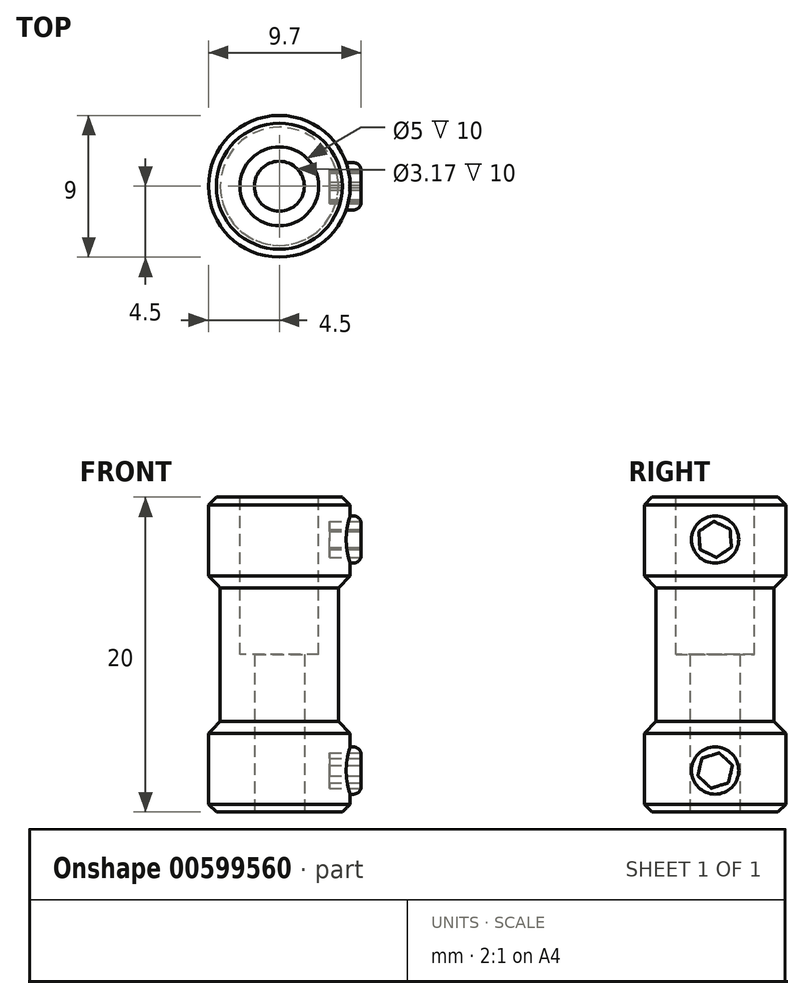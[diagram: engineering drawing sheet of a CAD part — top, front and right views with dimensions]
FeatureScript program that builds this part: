
annotation { "Feature Type Name" : "Feature", "Feature Type Description" : "" }
export const myFeature = defineFeature(function(context is Context, id is Id, definition is map)
    precondition{}
    {
        {
            var Q0;
            Q0=qCreatedBy(makeId("Top.planeOp"),FACE);
            var sketch = newSketch(context, id + "F0", { "sketchPlane" : qUnion([Q0])});
            skCircle(sketch, "E0", {"center": v(0, 0) * mm, "radius": 4.5 * mm});
            skSolve(sketch);
        }
        {
            var Q0;
            Q0 = qSketchRegion(id + "F0", true);
            extrude(context, id + "F1", {"entities" : qUnion([Q0]), "depth" : 20 * mm, "offsetDistance" : 25 * mm});
        }
        {
            var Q0;
            Q0=makeQuery(id+"F1.opExtrude","CAP_FACE",FACE,{"disambiguationData":[OSD([sQuery(id+"F0.wireOp",EDGE,"E0")])],"isStart":false});
            var sketch = newSketch(context, id + "F2", { "sketchPlane" : qUnion([Q0])});
            skCircle(sketch, "E1", {"center": v(0, 0) * mm, "radius": 2.5 * mm});
            skSolve(sketch);
        }
        {
            var Q0;
            Q0 = qSketchRegion(id + "F2", true);
            extrude(context, id + "F3", {"entities" : qUnion([Q0]), "operationType" : NewBodyOperationType.REMOVE, "oppositeDirection" : true, "depth" : 10 * mm, "offsetDistance" : 25 * mm});
        }
        {
            var Q0;
            Q0=makeQuery(id+"F1.opExtrude","CAP_FACE",FACE,{"disambiguationData":[OSD([sQuery(id+"F0.wireOp",EDGE,"E0")])],"isStart":true});
            var sketch = newSketch(context, id + "F4", { "sketchPlane" : qUnion([Q0])});
            skCircle(sketch, "E2", {"center": v(0, 0) * mm, "radius": 1.59 * mm});
            skSolve(sketch);
        }
        {
            var Q0;
            Q0 = qSketchRegion(id + "F4", true);
            extrude(context, id + "F5", {"entities" : qUnion([Q0]), "operationType" : NewBodyOperationType.REMOVE, "oppositeDirection" : true, "depth" : 10 * mm, "offsetDistance" : 25 * mm});
        }
        {
            var Q0;
            Q0=makeQuery(id+"F1.opExtrude","CAP_FACE",FACE,{"disambiguationData":[OSD([sQuery(id+"F0.wireOp",EDGE,"E0")])],"isStart":true});
            var sketch = newSketch(context, id + "F6", { "sketchPlane" : qUnion([Q0])});
            skCircle(sketch, "E3", {"center": v(0, 0) * mm, "radius": 3.75 * mm});
            skCircle(sketch, "E4", {"center": v(0, 0) * mm, "radius": 8.33 * mm});
            skSolve(sketch);
        }
        {
            var Q0;
            Q0 = qSketchRegion(id + "F6", true);
            extrude(context, id + "F7", {"entities" : qUnion([Q0]), "operationType" : NewBodyOperationType.REMOVE, "oppositeDirection" : true, "depth" : 14 * mm, "offsetDistance" : 25 * mm, "hasSecondDirection" : true, "secondDirectionOppositeDirection" : true, "secondDirectionDepth" : 6 * mm});
        }
        {
            var Q0;
            Q0=makeQuery(id+"F7.boolean.opBoolean","INTERSECT",EDGE,{"derivedFrom":[makeQuery(id+"F1.opExtrude","SWEPT_FACE",FACE,{"disambiguationData":[OSD([sQuery(id+"F0.wireOp",EDGE,"E0")])]}),makeQuery(id+"F7.opExtrude","CAP_FACE",FACE,{"disambiguationData":[OSD([sQuery(id+"F6.wireOp",EDGE,"E3"),sQuery(id+"F6.wireOp",EDGE,"E4")])],"isStart":false})]});
            var Q1;
            Q1=makeQuery(id+"F7.boolean.opBoolean","INTERSECT",EDGE,{"derivedFrom":[makeQuery(id+"F1.opExtrude","SWEPT_FACE",FACE,{"disambiguationData":[OSD([sQuery(id+"F0.wireOp",EDGE,"E0")])]}),makeQuery(id+"F7.opExtrude","CAP_FACE",FACE,{"disambiguationData":[OSD([sQuery(id+"F6.wireOp",EDGE,"E3"),sQuery(id+"F6.wireOp",EDGE,"E4")])],"isStart":true})]});
            chamfer(context, id + "F8", {"entities" : qUnion([Q0, Q1]), "width" : 1 * mm, "tangentPropagation" : true});
        }
        {
            var Q0;
            Q0=makeQuery(id+"F1.opExtrude","CAP_EDGE",EDGE,{"disambiguationData":[OSD([sQuery(id+"F0.wireOp",EDGE,"E0")])],"isStart":false});
            var Q1;
            Q1=makeQuery(id+"F1.opExtrude","CAP_EDGE",EDGE,{"disambiguationData":[OSD([sQuery(id+"F0.wireOp",EDGE,"E0")])],"isStart":true});
            chamfer(context, id + "F9", {"entities" : qUnion([Q0, Q1]), "width" : 0.5 * mm, "tangentPropagation" : true});
        }
        {
            var Q0;
            Q0=qCreatedBy(makeId("Right.planeOp"),FACE);
            var sketch = newSketch(context, id + "F10", { "sketchPlane" : qUnion([Q0])});
            skCircle(sketch, "E5", {"center": v(0, 17.31) * mm, "radius": 1.5 * mm});
            skCircle(sketch, "E6", {"center": v(0, 2.64) * mm, "radius": 1.5 * mm});
            skSolve(sketch);
        }
        {
            var Q0;
            Q0 = qSketchRegion(id + "F10", true);
            extrude(context, id + "F11", {"entities" : qUnion([Q0]), "operationType" : NewBodyOperationType.ADD, "depth" : 5.2 * mm, "offsetDistance" : 25 * mm, "hasSecondDirection" : true, "secondDirectionOppositeDirection" : false, "secondDirectionDepth" : 4 * mm});
        }
        {
            var Q0;
            Q0=makeQuery(id+"F11.opExtrude","CAP_FACE",FACE,{"disambiguationData":[OSD([sQuery(id+"F10.wireOp",EDGE,"E6")])],"isStart":false});
            var sketch = newSketch(context, id + "F12", { "sketchPlane" : qUnion([Q0])});
            skCircle(sketch, "E7.cCircle", {"center": v(0, 2.64) * mm, "radius": 1.15 * mm, "construction": true});
            skLineSegment(sketch, "E7.0", {"start": v(-0.84, 3.42) * mm, "end": v(0.26, 3.76) * mm});
            skLineSegment(sketch, "E7.1", {"start": v(0.26, 3.76) * mm, "end": v(1.1, 2.98) * mm});
            skLineSegment(sketch, "E7.2", {"start": v(1.1, 2.98) * mm, "end": v(0.84, 1.86) * mm});
            skLineSegment(sketch, "E7.3", {"start": v(0.84, 1.86) * mm, "end": v(-0.26, 1.52) * mm});
            skLineSegment(sketch, "E7.4", {"start": v(-0.26, 1.52) * mm, "end": v(-1.1, 2.3) * mm});
            skLineSegment(sketch, "E7.5", {"start": v(-1.1, 2.3) * mm, "end": v(-0.84, 3.42) * mm});
            skCircle(sketch, "E8.cCircle", {"center": v(0, 17.32) * mm, "radius": 1.15 * mm, "construction": true});
            skLineSegment(sketch, "E8.0", {"start": v(-1.03, 17.82) * mm, "end": v(-0.08, 18.47) * mm});
            skLineSegment(sketch, "E8.1", {"start": v(-0.08, 18.47) * mm, "end": v(0.95, 17.96) * mm});
            skLineSegment(sketch, "E8.2", {"start": v(0.95, 17.96) * mm, "end": v(1.03, 16.82) * mm});
            skLineSegment(sketch, "E8.3", {"start": v(1.03, 16.82) * mm, "end": v(0.08, 16.17) * mm});
            skLineSegment(sketch, "E8.4", {"start": v(0.08, 16.17) * mm, "end": v(-0.95, 16.67) * mm});
            skLineSegment(sketch, "E8.5", {"start": v(-0.95, 16.67) * mm, "end": v(-1.03, 17.82) * mm});
            skSolve(sketch);
        }
        {
            var Q0;
            Q0 = qSketchRegion(id + "F12", true);
            extrude(context, id + "F13", {"entities" : qUnion([Q0]), "operationType" : NewBodyOperationType.REMOVE, "oppositeDirection" : true, "depth" : 2 * mm, "offsetDistance" : 25 * mm});
        }
        {
            var Q0;
            Q0=makeQuery(id+"F11.opExtrude","CAP_EDGE",EDGE,{"disambiguationData":[OSD([sQuery(id+"F10.wireOp",EDGE,"E6")])],"isStart":false});
            var Q1;
            Q1=makeQuery(id+"F11.opExtrude","CAP_EDGE",EDGE,{"disambiguationData":[OSD([sQuery(id+"F10.wireOp",EDGE,"E5")])],"isStart":false});
            fillet(context, id + "F14", {"entities" : qUnion([Q0, Q1]), "radius" : 0.5 * mm, "tangentPropagation" : true, "allowEdgeOverflow" : false});
        }
    });
